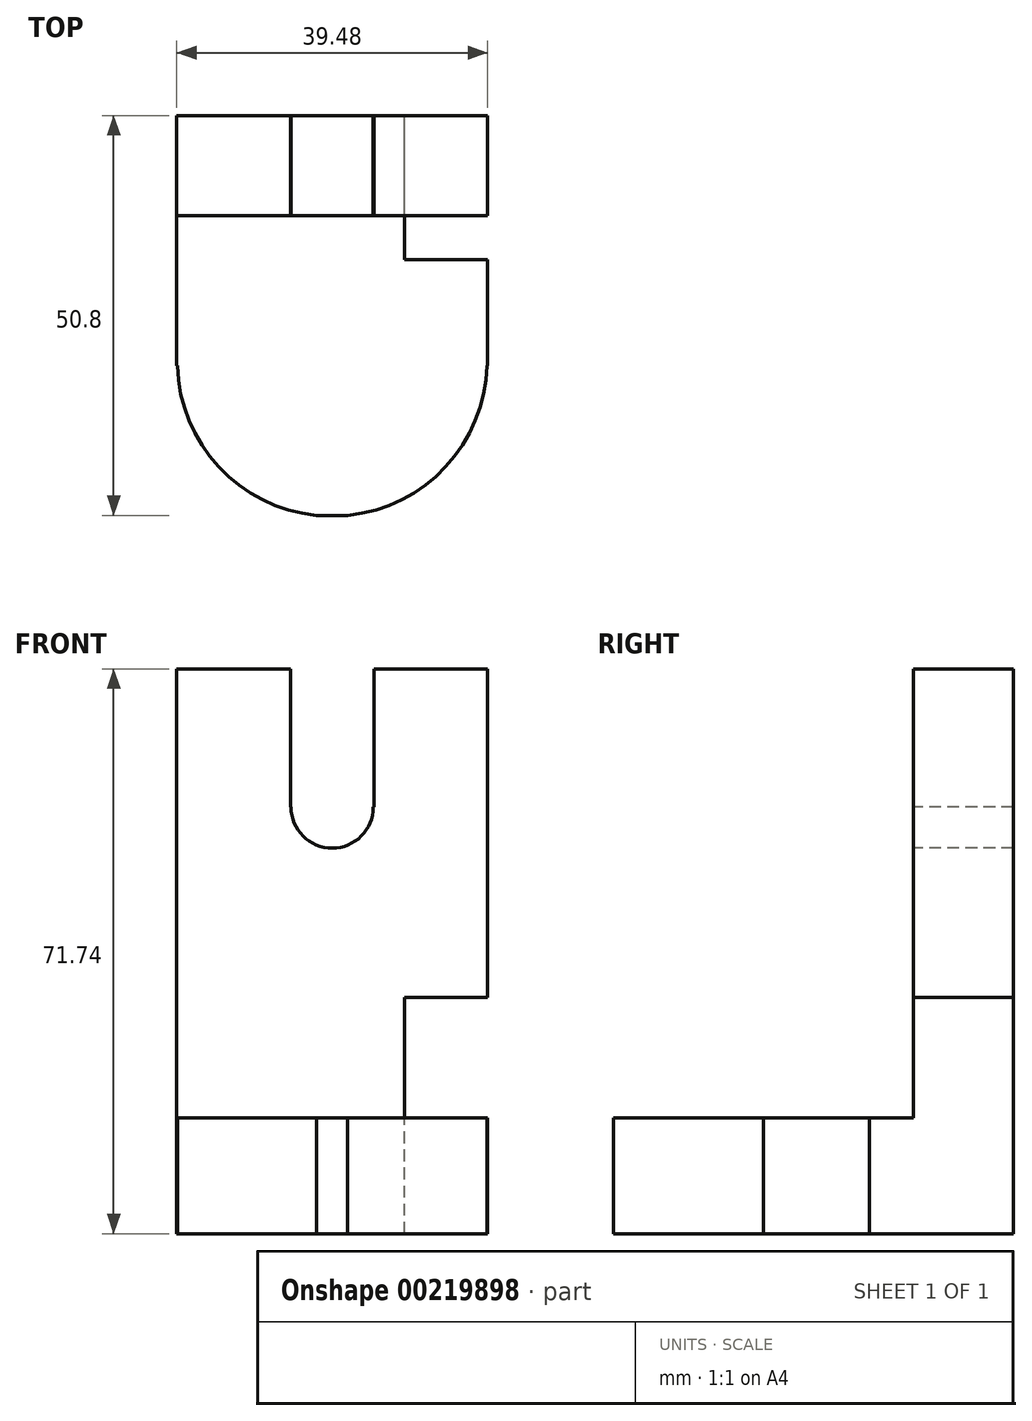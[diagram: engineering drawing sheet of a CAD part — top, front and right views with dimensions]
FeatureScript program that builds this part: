
annotation { "Feature Type Name" : "Feature", "Feature Type Description" : "" }
export const myFeature = defineFeature(function(context is Context, id is Id, definition is map)
    precondition{}
    {
        {
            var Q0;
            Q0=qCreatedBy(makeId("Front.planeOp"),FACE);
            var sketch = newSketch(context, id + "F0", { "sketchPlane" : qUnion([Q0])});
            skLineSegment(sketch, "E0.bottom", {"start": v(-19.74, 35.87) * mm, "end": v(19.74, 35.87) * mm});
            skLineSegment(sketch, "E0.top", {"start": v(-19.74, -35.87) * mm, "end": v(19.74, -35.87) * mm});
            skLineSegment(sketch, "E0.left", {"start": v(-19.74, 35.87) * mm, "end": v(-19.74, -35.87) * mm});
            skLineSegment(sketch, "E0.right", {"start": v(19.74, 35.87) * mm, "end": v(19.74, -35.87) * mm});
            skPoint(sketch, "E0.middle", {"position": v(0, 0) * mm});
            skSolve(sketch);
        }
        {
            var Q0;
            Q0=makeQuery(id+"F0.imprint","IMPRINT",FACE,{"disambiguationData":[TD([[makeQuery(id+"F0.imprint","IMPRINT",EDGE,{"derivedFrom":sQuery(id+"F0.wireOp",EDGE,"E0.bottom")}),-1.0]])]});
            extrude(context, id + "F1", {"entities" : qUnion([Q0]), "depth" : 12.7 * mm});
        }
        {
            var Q0;
            Q0=makeQuery(id+"F1.opExtrude","CAP_FACE",FACE,{"disambiguationData":[OSD([sQuery(id+"F0.wireOp",EDGE,"E0.bottom"),sQuery(id+"F0.wireOp",EDGE,"E0.top"),sQuery(id+"F0.wireOp",EDGE,"E0.left"),sQuery(id+"F0.wireOp",EDGE,"E0.right")])],"isStart":false});
            var sketch = newSketch(context, id + "F2", { "sketchPlane" : qUnion([Q0])});
            skLineSegment(sketch, "E1.bottom", {"start": v(-19.74, -35.87) * mm, "end": v(19.74, -35.87) * mm});
            skLineSegment(sketch, "E1.top", {"start": v(-19.74, -21.17) * mm, "end": v(19.74, -21.17) * mm});
            skLineSegment(sketch, "E1.left", {"start": v(-19.74, -35.87) * mm, "end": v(-19.74, -21.17) * mm});
            skLineSegment(sketch, "E1.right", {"start": v(19.74, -35.87) * mm, "end": v(19.74, -21.17) * mm});
            skSolve(sketch);
        }
        {
            var Q0;
            Q0 = qSketchRegion(id + "F2", true);
            extrude(context, id + "F3", {"entities" : qUnion([Q0]), "operationType" : NewBodyOperationType.ADD, "depth" : 38.1 * mm});
        }
        {
            var Q0;
            Q0=makeQuery(id+"F1.opExtrude","CAP_FACE",FACE,{"disambiguationData":[OSD([sQuery(id+"F0.wireOp",EDGE,"E0.bottom"),sQuery(id+"F0.wireOp",EDGE,"E0.top"),sQuery(id+"F0.wireOp",EDGE,"E0.left"),sQuery(id+"F0.wireOp",EDGE,"E0.right")])],"isStart":false});
            var sketch = newSketch(context, id + "F4", { "sketchPlane" : qUnion([Q0])});
            skLineSegment(sketch, "E2.bottom", {"start": v(-5.3, 18.32) * mm, "end": v(-5.22, 18.32) * mm});
            skLineSegment(sketch, "E2.top", {"start": v(-5.3, 53.42) * mm, "end": v(5.3, 53.42) * mm});
            skLineSegment(sketch, "E2.left", {"start": v(-5.3, 18.32) * mm, "end": v(-5.3, 53.42) * mm});
            skLineSegment(sketch, "E2.right", {"start": v(5.3, 18.32) * mm, "end": v(5.3, 53.42) * mm});
            skPoint(sketch, "E2.middle", {"position": v(0, 35.87) * mm});
            skArc(sketch, "E3", {"start": v(-5.22, 18.32) * mm, "mid": v(0, 13.1) * mm, "end": v(5.22, 18.32) * mm});
            skLineSegment(sketch, "E4.trimOffspring", {"start": v(5.22, 18.32) * mm, "end": v(5.3, 18.32) * mm});
            skSolve(sketch);
        }
        {
            var Q0;
            Q0 = qSketchRegion(id + "F4", true);
            extrude(context, id + "F5", {"entities" : qUnion([Q0]), "operationType" : NewBodyOperationType.REMOVE, "oppositeDirection" : true, "depth" : 25.4 * mm});
        }
        {
            var Q0;
            Q0=makeQuery(id+"F3.opExtrude","SWEPT_FACE",FACE,{"disambiguationData":[OSD([sQuery(id+"F2.wireOp",EDGE,"E1.top")])]});
            var sketch = newSketch(context, id + "F6", { "sketchPlane" : qUnion([Q0])});
            skArc(sketch, "E5", {"start": v(-19.66, -31.75) * mm, "mid": v(0, -50.9) * mm, "end": v(19.66, -31.75) * mm});
            skLineSegment(sketch, "E6", {"start": v(19.74, -31.75) * mm, "end": v(19.74, -50.8) * mm});
            skLineSegment(sketch, "E7", {"start": v(19.74, -50.8) * mm, "end": v(-19.74, -50.8) * mm});
            skLineSegment(sketch, "E8", {"start": v(-19.74, -50.8) * mm, "end": v(-19.74, -31.75) * mm});
            skLineSegment(sketch, "E9", {"start": v(-19.74, -31.75) * mm, "end": v(19.74, -31.75) * mm});
            skSolve(sketch);
        }
        {
            var Q0;
            {var subQ5=sQuery(id+"F6.wireOp",EDGE,"E8");Q0=makeQuery(id+"F6.imprint","IMPRINT",FACE,{"disambiguationData":[TD([[makeQuery(id+"F6.imprint","IMPRINT",EDGE,{"derivedFrom":subQ5}),-1.0]])]});}
            var Q1;
            {var subQ5=sQuery(id+"F6.wireOp",EDGE,"E6");Q1=makeQuery(id+"F6.imprint","IMPRINT",FACE,{"disambiguationData":[TD([[makeQuery(id+"F6.imprint","IMPRINT",EDGE,{"derivedFrom":subQ5}),1.0]])]});}
            extrude(context, id + "F7", {"entities" : qUnion([Q0, Q1]), "operationType" : NewBodyOperationType.REMOVE, "oppositeDirection" : true, "depth" : 25.4 * mm});
        }
        {
            var Q0;
            Q0=makeQuery(id+"F1.opExtrude","CAP_FACE",FACE,{"disambiguationData":[OSD([sQuery(id+"F0.wireOp",EDGE,"E0.bottom"),sQuery(id+"F0.wireOp",EDGE,"E0.top"),sQuery(id+"F0.wireOp",EDGE,"E0.left"),sQuery(id+"F0.wireOp",EDGE,"E0.right")])],"isStart":true});
            var sketch = newSketch(context, id + "F8", { "sketchPlane" : qUnion([Q0])});
            skLineSegment(sketch, "E10.bottom", {"start": v(-19.74, -35.87) * mm, "end": v(-9.16, -35.87) * mm});
            skLineSegment(sketch, "E10.top", {"start": v(-19.74, -5.87) * mm, "end": v(-9.16, -5.87) * mm});
            skLineSegment(sketch, "E10.left", {"start": v(-19.74, -35.87) * mm, "end": v(-19.74, -5.87) * mm});
            skLineSegment(sketch, "E10.right", {"start": v(-9.16, -35.87) * mm, "end": v(-9.16, -5.87) * mm});
            skSolve(sketch);
        }
        {
            var Q0;
            Q0=makeQuery(id+"F8.imprint","IMPRINT",FACE,{"disambiguationData":[TD([[makeQuery(id+"F8.imprint","IMPRINT",EDGE,{"derivedFrom":sQuery(id+"F8.wireOp",EDGE,"E10.bottom")}),-1.0]])]});
            extrude(context, id + "F9", {"entities" : qUnion([Q0]), "operationType" : NewBodyOperationType.REMOVE, "oppositeDirection" : true, "depth" : 18.29 * mm});
        }
    });
